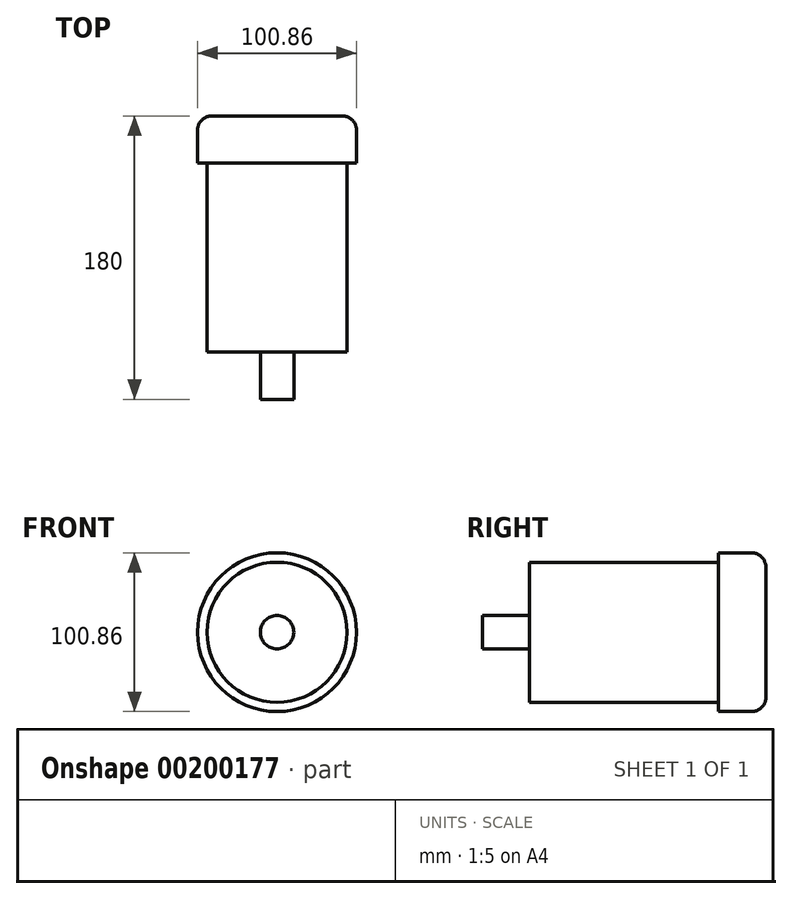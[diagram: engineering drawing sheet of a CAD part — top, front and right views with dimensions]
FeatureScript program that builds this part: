
annotation { "Feature Type Name" : "Feature", "Feature Type Description" : "" }
export const myFeature = defineFeature(function(context is Context, id is Id, definition is map)
    precondition{}
    {
        {
            var Q0;
            Q0=qCreatedBy(makeId("Front.planeOp"),FACE);
            var sketch = newSketch(context, id + "F0", { "sketchPlane" : qUnion([Q0])});
            skCircle(sketch, "E0", {"center": v(0, 0) * mm, "radius": 44.45 * mm});
            skSolve(sketch);
        }
        {
            var Q0;
            Q0 = qSketchRegion(id + "F0", true);
            extrude(context, id + "F1", {"entities" : qUnion([Q0]), "depth" : 120 * mm});
        }
        {
            var Q0;
            Q0=qCreatedBy(makeId("Front.planeOp"),FACE);
            var sketch = newSketch(context, id + "F2", { "sketchPlane" : qUnion([Q0])});
            skCircle(sketch, "E1", {"center": v(0, 0) * mm, "radius": 50.43 * mm});
            skSolve(sketch);
        }
        {
            var Q0;
            Q0=makeQuery(id+"F2.imprint","IMPRINT",FACE,{"disambiguationData":[TD([[makeQuery(id+"F2.imprint","IMPRINT",EDGE,{"derivedFrom":sQuery(id+"F2.wireOp",EDGE,"E1")}),1.0]])]});
            extrude(context, id + "F3", {"entities" : qUnion([Q0]), "operationType" : NewBodyOperationType.ADD, "oppositeDirection" : true, "depth" : 30 * mm});
        }
        {
            var Q0;
            Q0=makeQuery(id+"F3.opExtrude","CAP_FACE",FACE,{"disambiguationData":[OSD([sQuery(id+"F2.wireOp",EDGE,"E1")])],"isStart":false});
            fillet(context, id + "F4", {"entities" : qUnion([Q0]), "radius" : 9 * mm, "tangentPropagation" : true, "allowEdgeOverflow" : false});
        }
        {
            var Q0;
            Q0=qCreatedBy(makeId("Front.planeOp"),FACE);
            var sketch = newSketch(context, id + "F5", { "sketchPlane" : qUnion([Q0])});
            skCircle(sketch, "E2", {"center": v(0, 0) * mm, "radius": 10.64 * mm});
            skSolve(sketch);
        }
        {
            var Q0;
            Q0 = qSketchRegion(id + "F5", true);
            extrude(context, id + "F6", {"entities" : qUnion([Q0]), "operationType" : NewBodyOperationType.ADD, "depth" : 150 * mm});
        }
    });
